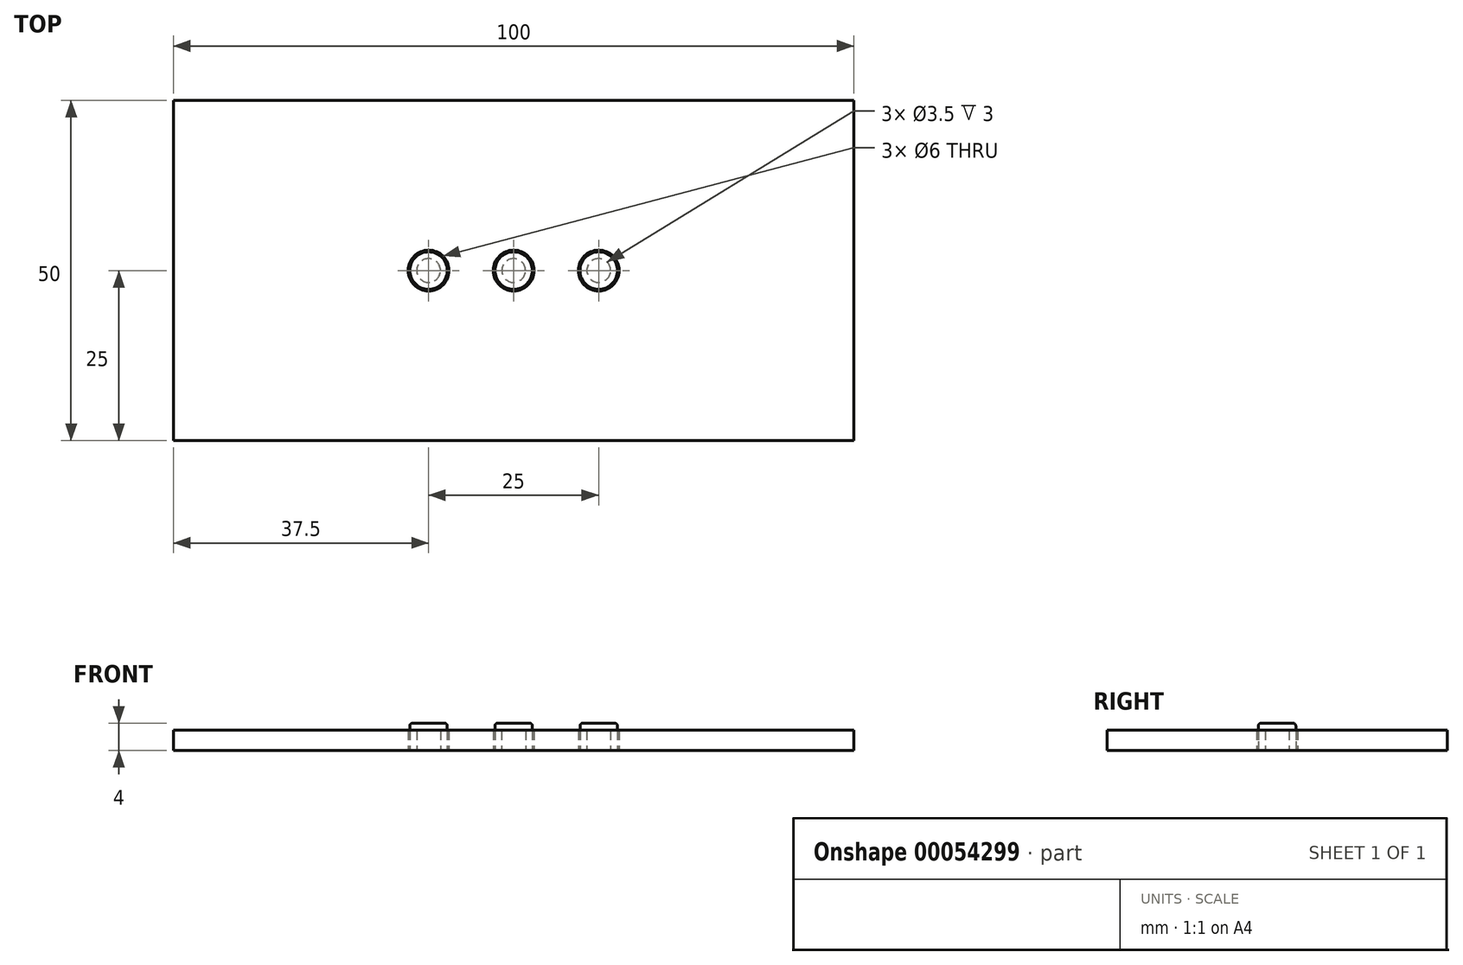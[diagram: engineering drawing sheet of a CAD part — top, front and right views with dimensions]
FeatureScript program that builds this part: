
annotation { "Feature Type Name" : "Feature", "Feature Type Description" : "" }
export const myFeature = defineFeature(function(context is Context, id is Id, definition is map)
    precondition{}
    {
        {
            var Q0;
            Q0=qCreatedBy(makeId("Top.planeOp"),FACE);
            var sketch = newSketch(context, id + "F0", { "sketchPlane" : qUnion([Q0])});
            skLineSegment(sketch, "E0.rect.bottom", {"start": v(50, 25) * mm, "end": v(-50, 25) * mm});
            skLineSegment(sketch, "E0.rect.top", {"start": v(50, -25) * mm, "end": v(-50, -25) * mm});
            skLineSegment(sketch, "E0.rect.left", {"start": v(50, 25) * mm, "end": v(50, -25) * mm});
            skLineSegment(sketch, "E0.rect.right", {"start": v(-50, 25) * mm, "end": v(-50, -25) * mm});
            skPoint(sketch, "E0.rect.middle", {"position": v(0, 0) * mm});
            skLineSegment(sketch, "E1", {"start": v(-50, 0) * mm, "end": v(50, 0) * mm, "construction": true});
            skCircle(sketch, "E2", {"center": v(-12.5, 0) * mm, "radius": 2.75 * mm});
            skCircle(sketch, "E3", {"center": v(-12.5, 0) * mm, "radius": 1.75 * mm});
            skCircle(sketch, "E4", {"center": v(-12.5, 0) * mm, "radius": 3 * mm});
            skCircle(sketch, "E5.1.0.0", {"center": v(0, 0) * mm, "radius": 1.75 * mm});
            skCircle(sketch, "E5.1.0.1", {"center": v(0, 0) * mm, "radius": 2.75 * mm});
            skCircle(sketch, "E5.1.0.2", {"center": v(0, 0) * mm, "radius": 3 * mm});
            skCircle(sketch, "E5.2.0.0", {"center": v(12.5, 0) * mm, "radius": 1.75 * mm});
            skCircle(sketch, "E5.2.0.1", {"center": v(12.5, 0) * mm, "radius": 2.75 * mm});
            skCircle(sketch, "E5.2.0.2", {"center": v(12.5, 0) * mm, "radius": 3 * mm});
            skLineSegment(sketch, "E5.direction1", {"start": v(-12.5, 0) * mm, "end": v(0, 0) * mm, "construction": true});
            skSolve(sketch);
        }
        {
            var Q0;
            Q0=makeQuery(id+"F0.imprint","IMPRINT",FACE,{"disambiguationData":[TD([[makeQuery(id+"F0.imprint","IMPRINT",EDGE,{"derivedFrom":sQuery(id+"F0.wireOp",EDGE,"E0.rect.bottom")}),1.0]])]});
            extrude(context, id + "F1", {"entities" : qUnion([Q0]), "depth" : 3 * mm});
        }
        {
            var Q0;
            Q0=makeQuery(id+"F0.imprint","IMPRINT",FACE,{"disambiguationData":[TD([[makeQuery(id+"F0.imprint","IMPRINT",EDGE,{"derivedFrom":sQuery(id+"F0.wireOp",EDGE,"E2")}),1.0]])]});
            var Q1;
            Q1=makeQuery(id+"F0.imprint","IMPRINT",FACE,{"disambiguationData":[TD([[makeQuery(id+"F0.imprint","IMPRINT",EDGE,{"derivedFrom":sQuery(id+"F0.wireOp",EDGE,"E3")}),1.0]])]});
            var Q2;
            Q2=makeQuery(id+"F0.imprint","IMPRINT",FACE,{"disambiguationData":[TD([[makeQuery(id+"F0.imprint","IMPRINT",EDGE,{"derivedFrom":sQuery(id+"F0.wireOp",EDGE,"E5.1.0.0")}),1.0]])]});
            var Q3;
            Q3=makeQuery(id+"F0.imprint","IMPRINT",FACE,{"disambiguationData":[TD([[makeQuery(id+"F0.imprint","IMPRINT",EDGE,{"derivedFrom":sQuery(id+"F0.wireOp",EDGE,"E5.1.0.0")}),-1.0]])]});
            var Q4;
            Q4=makeQuery(id+"F0.imprint","IMPRINT",FACE,{"disambiguationData":[TD([[makeQuery(id+"F0.imprint","IMPRINT",EDGE,{"derivedFrom":sQuery(id+"F0.wireOp",EDGE,"E5.2.0.0")}),1.0]])]});
            var Q5;
            Q5=makeQuery(id+"F0.imprint","IMPRINT",FACE,{"disambiguationData":[TD([[makeQuery(id+"F0.imprint","IMPRINT",EDGE,{"derivedFrom":sQuery(id+"F0.wireOp",EDGE,"E5.2.0.0")}),-1.0]])]});
            extrude(context, id + "F2", {"entities" : qUnion([Q0, Q1, Q2, Q3, Q4, Q5]), "depth" : 4 * mm});
        }
        {
            var Q0;
            Q0=makeQuery(id+"F0.imprint","IMPRINT",FACE,{"disambiguationData":[TD([[makeQuery(id+"F0.imprint","IMPRINT",EDGE,{"derivedFrom":sQuery(id+"F0.wireOp",EDGE,"E3")}),1.0]])]});
            var Q1;
            Q1=makeQuery(id+"F0.imprint","IMPRINT",FACE,{"disambiguationData":[TD([[makeQuery(id+"F0.imprint","IMPRINT",EDGE,{"derivedFrom":sQuery(id+"F0.wireOp",EDGE,"E5.1.0.0")}),1.0]])]});
            var Q2;
            Q2=makeQuery(id+"F0.imprint","IMPRINT",FACE,{"disambiguationData":[TD([[makeQuery(id+"F0.imprint","IMPRINT",EDGE,{"derivedFrom":sQuery(id+"F0.wireOp",EDGE,"E5.2.0.0")}),1.0]])]});
            extrude(context, id + "F3", {"entities" : qUnion([Q0, Q1, Q2]), "operationType" : NewBodyOperationType.REMOVE, "depth" : 3 * mm});
        }
        {
            var Q0;
            Q0=makeQuery(id+"F2.opExtrude","CAP_FACE",FACE,{"disambiguationData":[OSD([sQuery(id+"F0.wireOp",EDGE,"E5.2.0.1")])],"isStart":false});
            var Q1;
            Q1=makeQuery(id+"F2.opExtrude","CAP_FACE",FACE,{"disambiguationData":[OSD([sQuery(id+"F0.wireOp",EDGE,"E5.1.0.1")])],"isStart":false});
            var Q2;
            Q2=makeQuery(id+"F2.opExtrude","CAP_FACE",FACE,{"disambiguationData":[OSD([sQuery(id+"F0.wireOp",EDGE,"E2")])],"isStart":false});
            fillet(context, id + "F4", {"entities" : qUnion([Q0, Q1, Q2]), "radius" : 0.4 * mm, "tangentPropagation" : true, "allowEdgeOverflow" : false});
        }
    });
